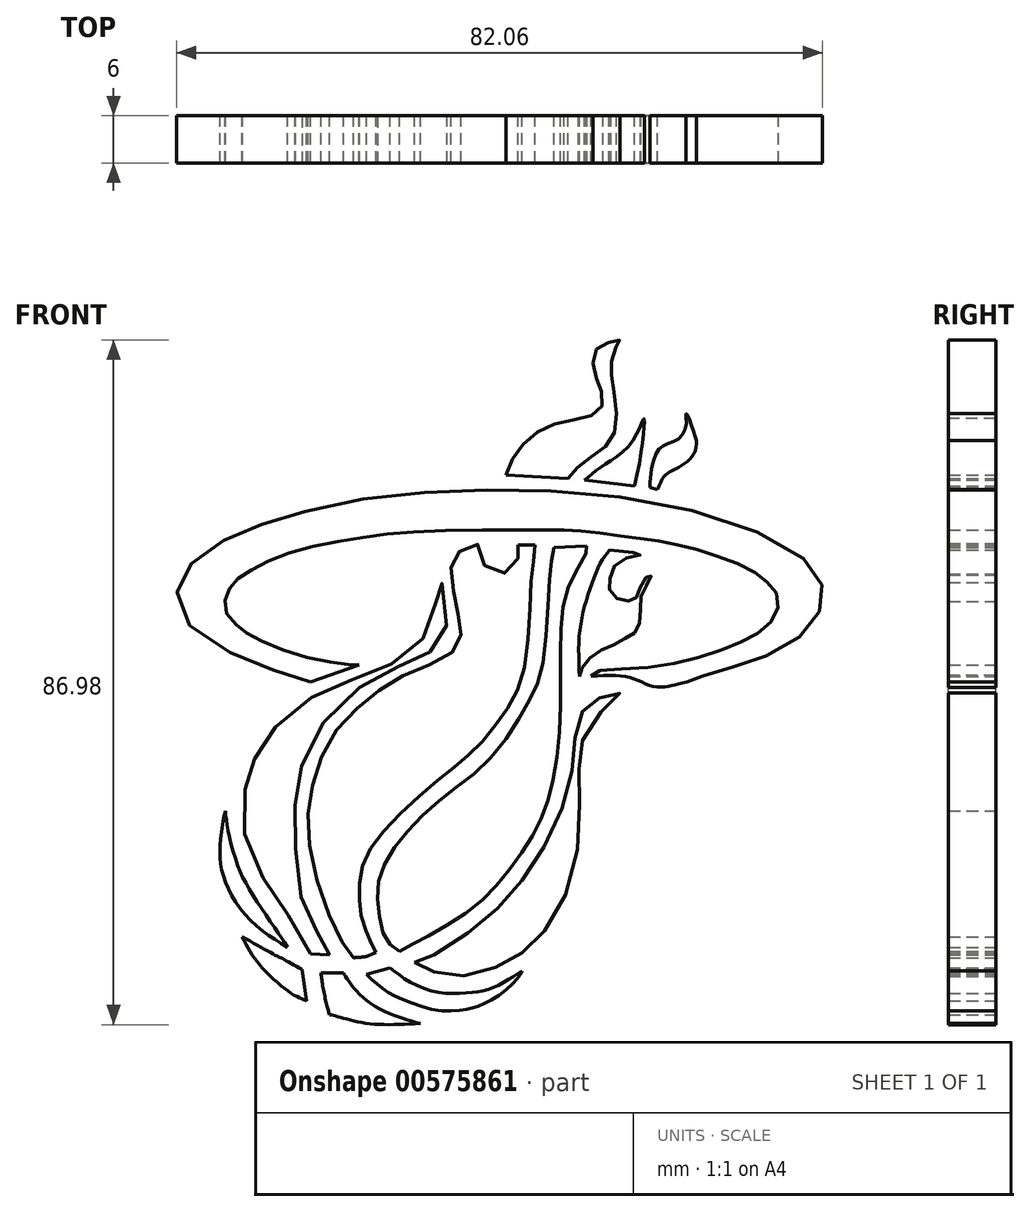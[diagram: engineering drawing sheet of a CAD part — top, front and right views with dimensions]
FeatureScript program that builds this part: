
annotation { "Feature Type Name" : "Feature", "Feature Type Description" : "" }
export const myFeature = defineFeature(function(context is Context, id is Id, definition is map)
    precondition{}
    {
        {
            var Q0;
            Q0=qCreatedBy(makeId("Front.planeOp"),FACE);
            var sketch = newSketch(context, id + "F0", { "sketchPlane" : qUnion([Q0])});
            skFitSpline(sketch, "E0", {"points": [v(-14.61, 2.57) * mm, v(-16.06, 2.69) * mm, v(-21.6, 3.68) * mm, v(-27.83, 6.03) * mm, v(-29.95, 7.46) * mm, v(-31.5, 9.39) * mm, v(-31.4, 11.48) * mm, v(-30.4, 13.18) * mm, v(-27.8, 14.92) * mm, v(-22.65, 17.05) * mm, v(-14.87, 18.7) * mm, v(-6.61, 19.55) * mm, v(11.47, 19.74) * mm], "startDerivative": vector(-17.87, 2.2) * mm, "endDerivative": vector(121.6, -0.45) * mm});
            skFitSpline(sketch, "E1", {"points": [v(27.05, 0.46) * mm, v(27.93, 0.75) * mm, v(28.74, 1.06) * mm, v(31.58, 1.93) * mm, v(35.32, 3.1) * mm, v(39.68, 4.96) * mm, v(43.22, 8.11) * mm, v(44.17, 10.48) * mm, v(44.13, 13.03) * mm, v(42.1, 15.91) * mm, v(32.07, 20.94) * mm, v(14.58, 24.36) * mm, v(0, 24.77) * mm, v(-13.18, 23.8) * mm, v(-24.11, 21.39) * mm, v(-29.45, 19.48) * mm, v(-34.85, 16.47) * mm, v(-37.13, 13.52) * mm, v(-37.6, 9.97) * mm, v(-32.98, 5.24) * mm, v(-25.85, 2.11) * mm, v(-20.75, 0.46) * mm], "startDerivative": vector(49.72, 22.99) * mm, "endDerivative": vector(114.44, -26.34) * mm});
            skLineSegment(sketch, "E2", {"start": v(-14.61, 2.57) * mm, "end": v(-20.75, 0.46) * mm});
            skFitSpline(sketch, "E3", {"points": [v(-31.57, -15.93) * mm, v(-32.2, -20.01) * mm, v(-32.1, -23.13) * mm, v(-30.77, -26.64) * mm, v(-27.57, -30.62) * mm, v(-23.65, -33.25) * mm], "startDerivative": vector(-5.02, -21.07) * mm, "endDerivative": vector(18.63, -10.9) * mm});
            skFitSpline(sketch, "E4", {"points": [v(-23.65, -33.25) * mm, v(-25.5, -30.5) * mm, v(-28.41, -26.08) * mm, v(-30.15, -22.43) * mm, v(-31.27, -18.11) * mm, v(-31.57, -15.93) * mm], "startDerivative": vector(-9.09, 13.58) * mm, "endDerivative": vector(-1.34, 12.9) * mm});
            skFitSpline(sketch, "E5", {"points": [v(-21.26, -40.05) * mm, v(-23.01, -39.23) * mm, v(-26.99, -35.73) * mm, v(-29.46, -31.97) * mm], "startDerivative": vector(-6.73, 2.7) * mm, "endDerivative": vector(-5.5, 10.44) * mm});
            skFitSpline(sketch, "E6", {"points": [v(-21.26, -40.05) * mm, v(-21.8, -36.1) * mm], "startDerivative": vector(-0.55, 4.04) * mm, "endDerivative": vector(-0.55, 4.04) * mm});
            skFitSpline(sketch, "E7", {"points": [v(-21.8, -36.1) * mm, v(-24.31, -34.7) * mm, v(-25.09, -34.34) * mm, v(-29.46, -31.97) * mm], "startDerivative": vector(-8.71, 4.06) * mm, "endDerivative": vector(-11.6, 5.73) * mm});
            skFitSpline(sketch, "E8", {"points": [v(-6.8, -42.95) * mm, v(-8.5, -42.47) * mm, v(-12, -41.07) * mm, v(-14.87, -38.89) * mm, v(-16.2, -37.15) * mm, v(-16.56, -36.53) * mm], "startDerivative": vector(-8.97, 1.95) * mm, "endDerivative": vector(-0.3, 4.71) * mm});
            skLineSegment(sketch, "E9", {"start": v(-16.56, -36.53) * mm, "end": v(-19.42, -36.53) * mm});
            skFitSpline(sketch, "E10", {"points": [v(-19.42, -36.53) * mm, v(-19.15, -38.42) * mm, v(-18.65, -40.73) * mm, v(-18.35, -41.83) * mm], "startDerivative": vector(0.64, -4.97) * mm, "endDerivative": vector(1.04, -3.62) * mm});
            skFitSpline(sketch, "E11", {"points": [v(-18.35, -41.83) * mm, v(-16.98, -42.16) * mm, v(-13.48, -42.95) * mm, v(-6.8, -42.95) * mm], "startDerivative": vector(5.91, -1.33) * mm, "endDerivative": vector(15.67, 0.82) * mm});
            skFitSpline(sketch, "E12", {"points": [v(6.12, -36.26) * mm, v(4.13, -37.52) * mm, v(1.92, -38.6) * mm, v(-0.48, -39.03) * mm, v(-4.05, -39.06) * mm, v(-8.08, -37.7) * mm, v(-10.65, -35.9) * mm], "startDerivative": vector(-12.84, -8.58) * mm, "endDerivative": vector(-11.86, 9.54) * mm});
            skFitSpline(sketch, "E13", {"points": [v(6.12, -36.26) * mm, v(5.74, -36.95) * mm, v(3.5, -39.17) * mm, v(0.68, -40.69) * mm, v(-1.03, -41.15) * mm, v(-4.64, -41.27) * mm, v(-9.51, -39.69) * mm, v(-11.81, -38.36) * mm, v(-13.64, -36.73) * mm], "startDerivative": vector(-2.1, -9.97) * mm, "endDerivative": vector(-14.28, 13.14) * mm});
            skLineSegment(sketch, "E14", {"start": v(-10.65, -35.9) * mm, "end": v(-13.64, -36.73) * mm});
            skFitSpline(sketch, "E15", {"points": [v(13.41, 1.1) * mm, v(13.71, 2.16) * mm, v(15.45, 4.04) * mm, v(17.64, 5.1) * mm, v(19.66, 6.17) * mm, v(20.75, 7.07) * mm, v(21.16, 9.52) * mm, v(21.33, 11.69) * mm, v(22.4, 13.52) * mm, v(22.46, 14.02) * mm, v(21.53, 13.32) * mm, v(20.86, 11.62) * mm, v(20.3, 10.89) * mm, v(18.68, 10.79) * mm, v(17.3, 12.05) * mm, v(17.36, 13.89) * mm, v(18.68, 15.92) * mm, v(21.2, 16.59) * mm, v(17.26, 17.22) * mm], "startDerivative": vector(5.24, 20.1) * mm, "endDerivative": vector(-74.95, 8.74) * mm});
            skFitSpline(sketch, "E16", {"points": [v(17.26, 17.22) * mm, v(16.22, 15.79) * mm, v(15.1, 13.22) * mm, v(13.99, 9.75) * mm, v(13.36, 5.85) * mm, v(13.41, 1.1) * mm], "startDerivative": vector(-7.18, -9.01) * mm, "endDerivative": vector(0.75, -19.69) * mm});
            skFitSpline(sketch, "E17", {"points": [v(-7.53, -35.16) * mm, v(-5.57, -36.22) * mm, v(-0.97, -36.9) * mm, v(4.36, -35.04) * mm, v(7.9, -32.46) * mm, v(12.27, -25) * mm, v(13.41, -14.3) * mm, v(13.41, -8.86) * mm, v(15.38, -4.16) * mm, v(18.52, -1.02) * mm, v(16.7, -1.33) * mm, v(14.32, -2.56) * mm, v(13, -5.7) * mm, v(12.45, -11.13) * mm, v(9.6, -19.26) * mm, v(4.96, -26.2) * mm, v(-0.4, -31.23) * mm, v(-6.66, -34.88) * mm, v(-7.53, -35.16) * mm]});
            skFitSpline(sketch, "E18", {"points": [v(-12.42, -33.9) * mm, v(-13.02, -32.72) * mm, v(-14.17, -29.84) * mm, v(-14.52, -26.43) * mm, v(-13.97, -22.34) * mm, v(-10.28, -17.22) * mm, v(-4.05, -11.64) * mm, v(0, -8.25) * mm, v(3.67, -3.82) * mm, v(6.39, 2) * mm, v(7.28, 13.22) * mm, v(7.77, 17.86) * mm], "startDerivative": vector(-12.11, 23.75) * mm, "endDerivative": vector(2.93, 46.79) * mm});
            skLineSegment(sketch, "E19", {"start": v(7.77, 17.86) * mm, "end": v(5.6, 17.86) * mm});
            skFitSpline(sketch, "E20", {"points": [v(5.6, 17.86) * mm, v(5.6, 16.93) * mm, v(5.08, 14.9) * mm, v(1.78, 14.57) * mm, v(0.56, 17.86) * mm, v(-1.7, 17.12) * mm, v(-2.88, 15.19) * mm, v(-2.46, 11.5) * mm, v(-1.85, 8.16) * mm, v(-1.8, 5.38) * mm, v(-4.49, 3.12) * mm, v(-9.53, 0.95) * mm, v(-13.73, -1.98) * mm, v(-17.88, -6.27) * mm, v(-20.29, -12.02) * mm, v(-21.09, -17.59) * mm, v(-19.67, -25.58) * mm, v(-16.84, -32.38) * mm, v(-15.28, -34.63) * mm], "startDerivative": vector(-0.65, -35.27) * mm, "endDerivative": vector(32.2, -41.36) * mm});
            skFitSpline(sketch, "E21", {"points": [v(-15.28, -34.63) * mm, v(-13.7, -34.44) * mm, v(-12.42, -33.9) * mm], "startDerivative": vector(2.96, 0.63) * mm, "endDerivative": vector(2.66, 1.2) * mm});
            skFitSpline(sketch, "E22", {"points": [v(-18.33, -34.2) * mm, v(-19.34, -32.27) * mm, v(-20.67, -30.04) * mm, v(-22.42, -25) * mm, v(-22.65, -17.8) * mm, v(-22.61, -13.47) * mm, v(-20.95, -7.92) * mm, v(-16.53, -1.8) * mm, v(-10.93, 1.7) * mm, v(-7.17, 3.52) * mm, v(-4.55, 4.96) * mm, v(-3.44, 8.48) * mm, v(-4.2, 13.08) * mm, v(-4.63, 12.6) * mm, v(-4.95, 9.51) * mm, v(-6.73, 5.62) * mm, v(-10.62, 2.65) * mm, v(-15.9, 0.55) * mm, v(-21.05, -1.83) * mm, v(-25.84, -6.07) * mm, v(-27.9, -9.52) * mm, v(-28.8, -12.15) * mm, v(-29.36, -17.37) * mm, v(-27.18, -23.76) * mm, v(-23.81, -28.87) * mm, v(-20.73, -34.14) * mm], "startDerivative": vector(-34.85, 71.05) * mm, "endDerivative": vector(64.16, -116.3) * mm});
            skLineSegment(sketch, "E23", {"start": v(-20.73, -34.14) * mm, "end": v(-18.33, -34.2) * mm});
            skFitSpline(sketch, "E24", {"points": [v(14.05, 26.07) * mm, v(16.13, 27.75) * mm, v(19.99, 30.8) * mm, v(21.6, 33.9) * mm, v(21.64, 33.6) * mm, v(20.4, 25.3) * mm], "startDerivative": vector(11.44, 8.12) * mm, "endDerivative": vector(-8.13, -33.64) * mm});
            skLineSegment(sketch, "E25", {"start": v(20.4, 25.3) * mm, "end": v(14.05, 26.07) * mm});
            skFitSpline(sketch, "E26", {"points": [v(11.98, 26.29) * mm, v(13.72, 28.17) * mm, v(16.77, 30.43) * mm, v(18.13, 33.56) * mm, v(17.59, 38.67) * mm, v(17.45, 40.9) * mm, v(18.25, 43.32) * mm, v(18.56, 43.85) * mm, v(17.22, 43.57) * mm, v(15.39, 42.5) * mm, v(15.37, 39.7) * mm, v(16.19, 37.4) * mm, v(16.12, 35.13) * mm, v(12.95, 33.77) * mm, v(8.91, 32.69) * mm, v(5.66, 29.94) * mm, v(4.1, 26.72) * mm], "startDerivative": vector(25.03, 30.96) * mm, "endDerivative": vector(-17.66, -47.14) * mm});
            skLineSegment(sketch, "E27", {"start": v(4.1, 26.72) * mm, "end": v(11.98, 26.29) * mm});
            skFitSpline(sketch, "E28", {"points": [v(23.32, 24.9) * mm, v(23.77, 25.85) * mm, v(24.55, 26.92) * mm, v(27.13, 28.43) * mm, v(28.25, 31.13) * mm], "startDerivative": vector(2.4, 5.13) * mm, "endDerivative": vector(-1.66, 9.96) * mm});
            skFitSpline(sketch, "E29", {"points": [v(28.25, 31.13) * mm, v(27.7, 32.98) * mm, v(26.96, 34.55) * mm, v(26.96, 33.03) * mm, v(25.67, 31.13) * mm, v(23.66, 30.17) * mm, v(22.76, 28.2) * mm, v(22.48, 26.75) * mm, v(22.37, 25.13) * mm], "startDerivative": vector(-3.36, 12.99) * mm, "endDerivative": vector(-0.66, -14.39) * mm});
            skLineSegment(sketch, "E30", {"start": v(23.32, 24.9) * mm, "end": v(22.37, 25.13) * mm});
            skFitSpline(sketch, "E31", {"points": [v(-9.46, -33.8) * mm, v(-5.93, -31.88) * mm, v(0, -28.21) * mm, v(4.34, -23.61) * mm, v(7.75, -18.55) * mm, v(9.8, -13.24) * mm, v(10.93, -4.6) * mm, v(11, 5.53) * mm, v(12.08, 12.7) * mm, v(14.32, 16.93) * mm, v(14.32, 17.72) * mm], "startDerivative": vector(38.6, 21.19) * mm, "endDerivative": vector(-4.05, 15.9) * mm});
            skLineSegment(sketch, "E32", {"start": v(14.32, 17.72) * mm, "end": v(10.16, 17.52) * mm});
            skFitSpline(sketch, "E33", {"points": [v(-9.46, -33.8) * mm, v(-11.06, -32.44) * mm, v(-12.1, -28.76) * mm, v(-11.9, -24.12) * mm, v(-9.08, -19.32) * mm, v(-4.05, -14.33) * mm, v(1.75, -9.66) * mm, v(6.6, -2.72) * mm, v(8.72, 2.6) * mm, v(9.66, 13.84) * mm, v(10.16, 17.52) * mm], "startDerivative": vector(-29.03, 17.82) * mm, "endDerivative": vector(6.47, 36.84) * mm});
            skFitSpline(sketch, "E34", {"points": [v(11.47, 19.74) * mm, v(14.58, 19.5) * mm, v(18.9, 18.95) * mm, v(22.7, 18.47) * mm, v(26.55, 17.71) * mm, v(30.57, 16.55) * mm, v(35.06, 14.73) * mm, v(37.24, 13.16) * mm, v(38.56, 11.45) * mm, v(38.42, 9.18) * mm, v(36.46, 6.88) * mm, v(33.2, 5.17) * mm, v(27.8, 3.32) * mm, v(20.85, 2.18) * mm, v(15.68, 1.78) * mm, v(14.9, 1.17) * mm], "startDerivative": vector(47.99, -2.67) * mm, "endDerivative": vector(-16.36, -19.4) * mm});
            skFitSpline(sketch, "E35", {"points": [v(27.05, 0.46) * mm, v(25.27, 0) * mm, v(24.72, -0.13) * mm, v(23.1, -0.2) * mm, v(21.25, 0.46) * mm, v(19.05, 1.14) * mm, v(14.9, 1.17) * mm], "startDerivative": vector(-13.2, -3.67) * mm, "endDerivative": vector(-18.56, -0.84) * mm});
            skSolve(sketch);
        }
        {
            var Q0;
            Q0=makeQuery(id+"F0.imprint","IMPRINT",FACE,{"disambiguationData":[TD([[makeQuery(id+"F0.imprint","IMPRINT",EDGE,{"derivedFrom":sQuery(id+"F0.wireOp",EDGE,"E0")}),1.0]])]});
            var Q1;
            Q1=makeQuery(id+"F0.imprint","IMPRINT",FACE,{"disambiguationData":[TD([[makeQuery(id+"F0.imprint","IMPRINT",EDGE,{"derivedFrom":sQuery(id+"F0.wireOp",EDGE,"E3")}),1.0]])]});
            var Q2;
            Q2=makeQuery(id+"F0.imprint","IMPRINT",FACE,{"disambiguationData":[TD([[makeQuery(id+"F0.imprint","IMPRINT",EDGE,{"derivedFrom":sQuery(id+"F0.wireOp",EDGE,"E5")}),-1.0]])]});
            var Q3;
            Q3=makeQuery(id+"F0.imprint","IMPRINT",FACE,{"disambiguationData":[TD([[makeQuery(id+"F0.imprint","IMPRINT",EDGE,{"derivedFrom":sQuery(id+"F0.wireOp",EDGE,"E8")}),1.0]])]});
            var Q4;
            Q4=makeQuery(id+"F0.imprint","IMPRINT",FACE,{"disambiguationData":[TD([[makeQuery(id+"F0.imprint","IMPRINT",EDGE,{"derivedFrom":sQuery(id+"F0.wireOp",EDGE,"E12")}),1.0]])]});
            var Q5;
            Q5=makeQuery(id+"F0.imprint","IMPRINT",FACE,{"disambiguationData":[TD([[makeQuery(id+"F0.imprint","IMPRINT",EDGE,{"derivedFrom":sQuery(id+"F0.wireOp",EDGE,"E15")}),1.0]])]});
            var Q6;
            Q6=makeQuery(id+"F0.imprint","IMPRINT",FACE,{"disambiguationData":[TD([[makeQuery(id+"F0.imprint","IMPRINT",EDGE,{"derivedFrom":sQuery(id+"F0.wireOp",EDGE,"E17")}),1.0]])]});
            var Q7;
            Q7=makeQuery(id+"F0.imprint","IMPRINT",FACE,{"disambiguationData":[TD([[makeQuery(id+"F0.imprint","IMPRINT",EDGE,{"derivedFrom":sQuery(id+"F0.wireOp",EDGE,"E18")}),1.0]])]});
            var Q8;
            Q8=makeQuery(id+"F0.imprint","IMPRINT",FACE,{"disambiguationData":[TD([[makeQuery(id+"F0.imprint","IMPRINT",EDGE,{"derivedFrom":sQuery(id+"F0.wireOp",EDGE,"E22")}),1.0]])]});
            var Q9;
            Q9=makeQuery(id+"F0.imprint","IMPRINT",FACE,{"disambiguationData":[TD([[makeQuery(id+"F0.imprint","IMPRINT",EDGE,{"derivedFrom":sQuery(id+"F0.wireOp",EDGE,"E24")}),-1.0]])]});
            var Q10;
            Q10=makeQuery(id+"F0.imprint","IMPRINT",FACE,{"disambiguationData":[TD([[makeQuery(id+"F0.imprint","IMPRINT",EDGE,{"derivedFrom":sQuery(id+"F0.wireOp",EDGE,"E26")}),1.0]])]});
            var Q11;
            Q11=makeQuery(id+"F0.imprint","IMPRINT",FACE,{"disambiguationData":[TD([[makeQuery(id+"F0.imprint","IMPRINT",EDGE,{"derivedFrom":sQuery(id+"F0.wireOp",EDGE,"E28")}),1.0]])]});
            var Q12;
            Q12=makeQuery(id+"F0.imprint","IMPRINT",FACE,{"disambiguationData":[TD([[makeQuery(id+"F0.imprint","IMPRINT",EDGE,{"derivedFrom":sQuery(id+"F0.wireOp",EDGE,"E31")}),1.0]])]});
            extrude(context, id + "F1", {"entities" : qUnion([Q0, Q1, Q2, Q3, Q4, Q5, Q6, Q7, Q8, Q9, Q10, Q11, Q12]), "depth" : 6 * mm, "offsetDistance" : 25 * mm});
        }
    });
